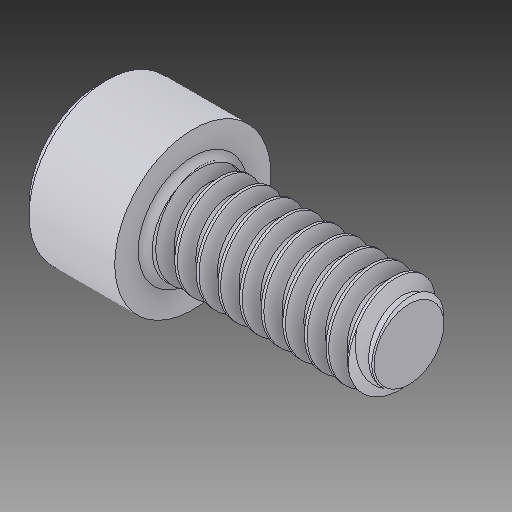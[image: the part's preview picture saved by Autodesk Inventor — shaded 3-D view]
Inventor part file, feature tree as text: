
AUTODESK INVENTOR PART (.ipt)
format: ipt  version: 2018 (Build 220112000, 112)  size: 504,832 bytes
history: native  units: in
note: dims shown in document units (in); Inventor stores cm internally (conversion verified against a paired STEP export)
features: thread x1
ambient origin geometry x8: Origin, YZ Plane, XZ Plane, XY Plane, X Axis, Y Axis, Z Axis, Center Point
bodies: Solid1 (feature_tree)
feature tree (1):
  thread  "Thread1"  [1 undecoded]
note: 1 required parameter value undecoded (feature->parameter linkage not recoverable at this tier; creation-order binding heuristic only, values carry confidence <= 0.55)
